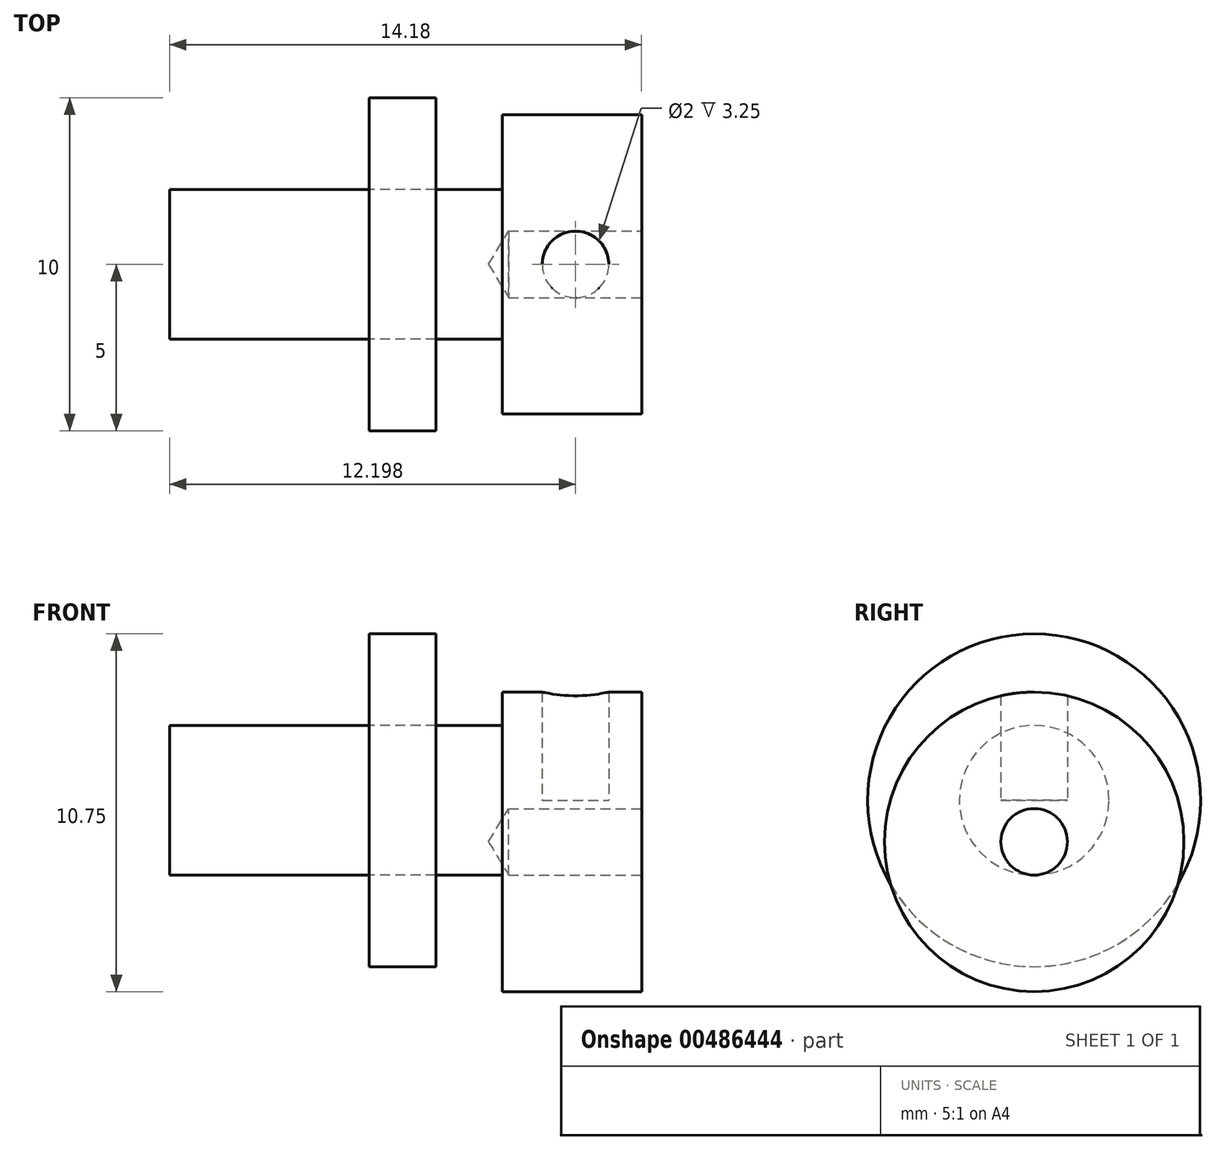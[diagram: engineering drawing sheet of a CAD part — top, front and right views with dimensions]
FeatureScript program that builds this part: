
annotation { "Feature Type Name" : "Feature", "Feature Type Description" : "" }
export const myFeature = defineFeature(function(context is Context, id is Id, definition is map)
    precondition{}
    {
        {
            var Q0;
            Q0=qCreatedBy(makeId("Front.planeOp"),FACE);
            var sketch = newSketch(context, id + "F0", { "sketchPlane" : qUnion([Q0])});
            skLineSegment(sketch, "E0.bottom", {"start": v(-7.95, 0) * mm, "end": v(2.05, 0) * mm});
            skLineSegment(sketch, "E0.top", {"start": v(-7.95, 2.25) * mm, "end": v(2.05, 2.25) * mm});
            skLineSegment(sketch, "E0.left", {"start": v(-7.95, 0) * mm, "end": v(-7.95, 2.25) * mm});
            skLineSegment(sketch, "E0.right", {"start": v(2.05, 0) * mm, "end": v(2.05, 2.25) * mm});
            skSolve(sketch);
        }
        {
            var Q0;
            Q0=qCreatedBy(makeId("Front.planeOp"),FACE);
            var sketch = newSketch(context, id + "F1", { "sketchPlane" : qUnion([Q0])});
            skLineSegment(sketch, "E1.bottom", {"start": v(-1.95, 5) * mm, "end": v(0.05, 5) * mm});
            skLineSegment(sketch, "E1.top", {"start": v(-1.95, 0) * mm, "end": v(0.05, 0) * mm});
            skLineSegment(sketch, "E1.left", {"start": v(-1.95, 5) * mm, "end": v(-1.95, 0) * mm});
            skLineSegment(sketch, "E1.right", {"start": v(0.05, 5) * mm, "end": v(0.05, 0) * mm});
            skSolve(sketch);
        }
        {
            var Q0;
            Q0=qCreatedBy(makeId("Front.planeOp"),FACE);
            var sketch = newSketch(context, id + "F2", { "sketchPlane" : qUnion([Q0])});
            skLineSegment(sketch, "E2.bottom", {"start": v(2.05, 3.25) * mm, "end": v(6.23, 3.25) * mm});
            skLineSegment(sketch, "E2.top", {"start": v(2.05, -1.25) * mm, "end": v(6.23, -1.25) * mm});
            skLineSegment(sketch, "E2.left", {"start": v(2.05, 3.25) * mm, "end": v(2.05, -1.25) * mm});
            skLineSegment(sketch, "E2.right", {"start": v(6.23, 3.25) * mm, "end": v(6.23, -1.25) * mm});
            skSolve(sketch);
        }
        {
            var Q0;
            Q0=makeQuery(id+"F0.imprint","IMPRINT",FACE,{"disambiguationData":[TD([[makeQuery(id+"F0.imprint","IMPRINT",EDGE,{"derivedFrom":sQuery(id+"F0.wireOp",EDGE,"E0.bottom")}),1.0]])]});
            var Q1;
            Q1=makeQuery(id+"F1.imprint","IMPRINT",FACE,{"disambiguationData":[TD([[makeQuery(id+"F1.imprint","IMPRINT",EDGE,{"derivedFrom":sQuery(id+"F1.wireOp",EDGE,"E1.bottom")}),-1.0]])]});
            var Q2;
            Q2=sQuery(id+"F0.wireOp",EDGE,"E0.bottom");
            revolve(context, id + "F3", {"entities" : qUnion([Q0, Q1]), "axis" : qUnion([Q2]), "revolveType" : RevolveType.FULL});
        }
        {
            var Q0;
            Q0=makeQuery(id+"F2.imprint","IMPRINT",FACE,{"disambiguationData":[TD([[makeQuery(id+"F2.imprint","IMPRINT",EDGE,{"derivedFrom":sQuery(id+"F2.wireOp",EDGE,"E2.bottom")}),-1.0]])]});
            var Q1;
            Q1=sQuery(id+"F2.wireOp",EDGE,"E2.top");
            revolve(context, id + "F4", {"operationType" : NewBodyOperationType.ADD, "entities" : qUnion([Q0]), "axis" : qUnion([Q1]), "revolveType" : RevolveType.FULL});
        }
        {
            var Q0;
            Q0=makeQuery(id+"F4.opRevolve","SWEPT_FACE",FACE,{"disambiguationData":[OSD([sQuery(id+"F2.wireOp",EDGE,"E2.right")])]});
            var sketch = newSketch(context, id + "F5", { "sketchPlane" : qUnion([Q0])});
            skPoint(sketch, "E3", {"position": v(0, -1.25) * mm});
            skSolve(sketch);
        }
        {
            var Q0;
            Q0=sQuery(id+"F5.wireOp",VERTEX,"E3");
            var Q1;
            Q1=makeQuery(id+"F3.opRevolve","SWEPT_BODY",BODY,{"disambiguationData":[OSD([sQuery(id+"F0.wireOp",EDGE,"E0.bottom"),sQuery(id+"F0.wireOp",EDGE,"E0.top"),sQuery(id+"F0.wireOp",EDGE,"E0.left"),sQuery(id+"F0.wireOp",EDGE,"E0.right")])]});
            hole(context, id + "F6", {"style" : HoleStyle.SIMPLE, "endStyle" : HoleEndStyle.BLIND, "holeDiameter" : 2 * mm, "holeDepth" : 4 * mm, "isTappedThrough" : true, "tappedDepth" : 12 * mm, "tapClearance" : 3, "locations" : qUnion([Q0]), "scope" : qUnion([Q1])});
        }
        {
            var Q0;
            Q0=qCreatedBy(makeId("Top.planeOp"),FACE);
            var sketch = newSketch(context, id + "F7", { "sketchPlane" : qUnion([Q0])});
            skPoint(sketch, "E4", {"position": v(4.25, 0) * mm});
            skSolve(sketch);
        }
        {
            var Q0;
            Q0=sQuery(id+"F7.wireOp",VERTEX,"E4");
            var Q1;
            Q1=makeQuery(id+"F3.opRevolve","SWEPT_BODY",BODY,{"disambiguationData":[OSD([sQuery(id+"F0.wireOp",EDGE,"E0.bottom"),sQuery(id+"F0.wireOp",EDGE,"E0.top"),sQuery(id+"F0.wireOp",EDGE,"E0.left"),sQuery(id+"F0.wireOp",EDGE,"E0.right")])]});
            hole(context, id + "F8", {"style" : HoleStyle.SIMPLE, "endStyle" : HoleEndStyle.BLIND, "oppositeDirection" : true, "holeDiameter" : 2 * mm, "holeDepth" : 5 * mm, "isTappedThrough" : true, "tappedDepth" : 12 * mm, "tapClearance" : 3, "locations" : qUnion([Q0]), "scope" : qUnion([Q1])});
        }
    });
